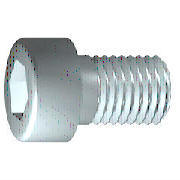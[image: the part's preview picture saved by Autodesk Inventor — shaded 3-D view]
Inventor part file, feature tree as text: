
AUTODESK INVENTOR PART (.ipt)
format: ipt  version: 2020 (Build 240168000, 168)  size: 194,560 bytes
history: native  units: mm (DEFAULTED — no unit token found)
features: sketch x2, extrude x1, plane x1, fillet x1
ambient origin geometry x7: Origin, YZ Plane, XY Plane, X Axis, Y Axis, Z Axis, Center Point
bodies: Solid1 (feature_tree), Body (feature_tree)
feature tree (5):
  extrude  "Slot"  Depth=3.0mm
  plane  "Work Plane1"
  fillet  "Fillet2"  Radius=3.0mm
  sketch  "Sketch1"  dims[d1=10.75mm d2=0.306825mm d3=3.0mm]
  sketch  "Sketch2"  dims[d4=1.3mm d5=60.0deg d6=3.0mm d7=3.0mm d8=2.886751mm d9=5.5mm d10=90.0deg d11=10.0mm d12=0.0mm d13=10.75mm d14=0.0mm d15=0.306725mm d16=0.306725mm d17=0.3mm d19=0.0mm d26=12.0mm d27=45.0deg d28=0.0mm d29=0.0mm d30=0.1mm]
